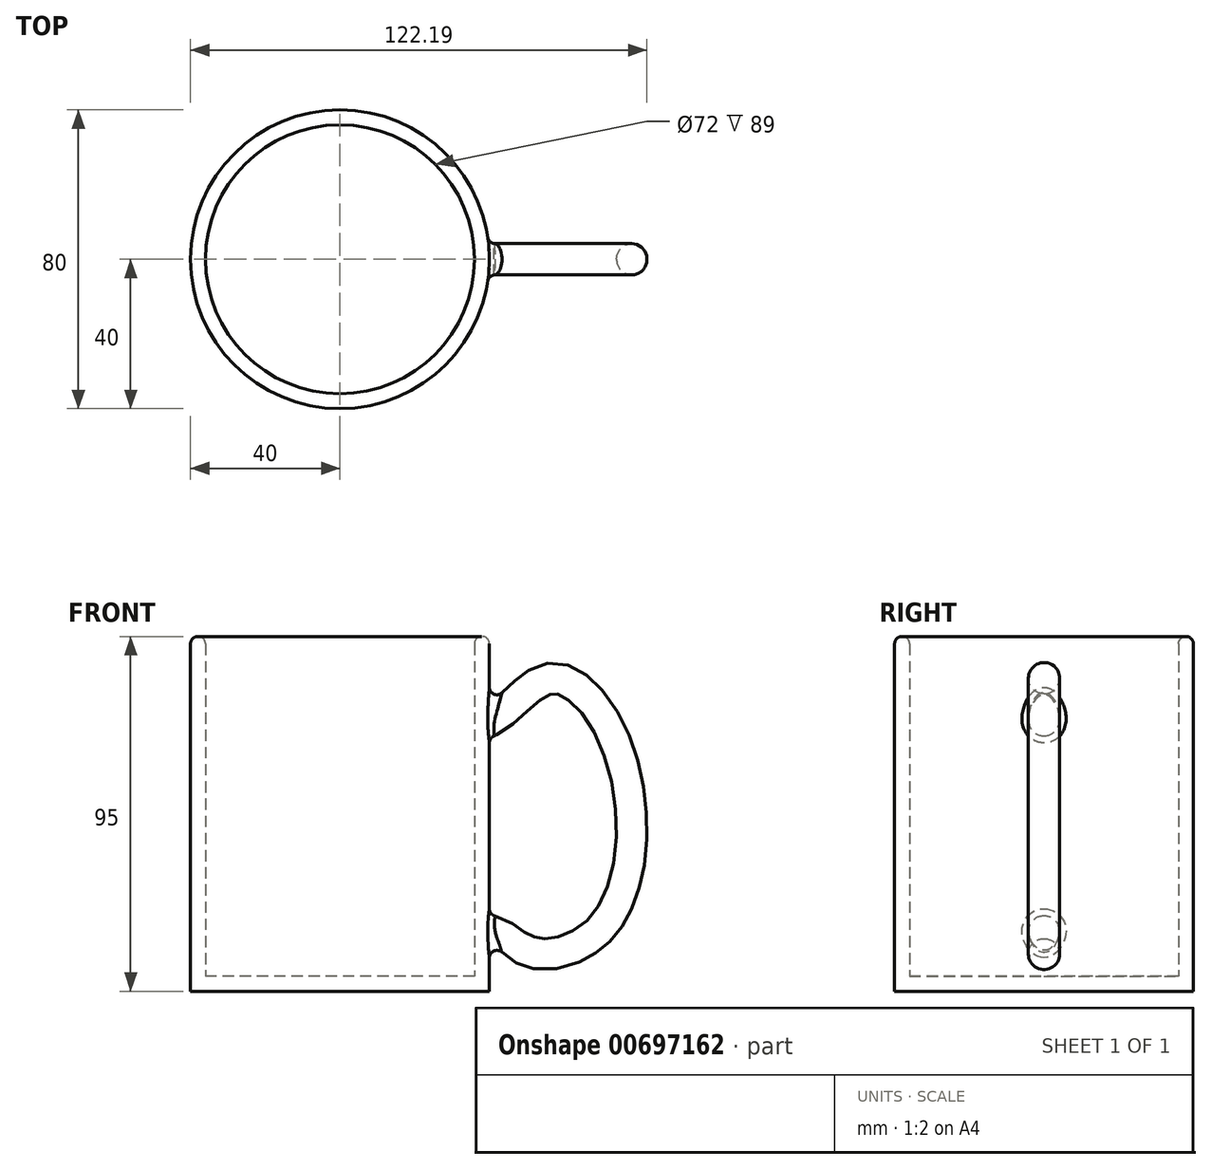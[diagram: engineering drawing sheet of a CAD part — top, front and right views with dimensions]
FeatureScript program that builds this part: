
annotation { "Feature Type Name" : "Feature", "Feature Type Description" : "" }
export const myFeature = defineFeature(function(context is Context, id is Id, definition is map)
    precondition{}
    {
        {
            var Q0;
            Q0=qCreatedBy(makeId("Top.planeOp"),FACE);
            var sketch = newSketch(context, id + "F0", { "sketchPlane" : qUnion([Q0])});
            skCircle(sketch, "E0", {"center": v(0, 0) * mm, "radius": 40 * mm});
            skSolve(sketch);
        }
        {
            var Q0;
            Q0 = qSketchRegion(id + "F0", true);
            extrude(context, id + "F1", {"entities" : qUnion([Q0]), "depth" : 95 * mm, "offsetDistance" : 25 * mm});
        }
        {
            var Q0;
            Q0=qCreatedBy(makeId("Front.planeOp"),FACE);
            var sketch = newSketch(context, id + "F2", { "sketchPlane" : qUnion([Q0])});
            skFitSpline(sketch, "E1", {"points": [v(32.9, 72.73) * mm, v(40.58, 72.94) * mm, v(56.34, 84.02) * mm, v(75.3, 63.57) * mm, v(71.46, 18.2) * mm, v(51.23, 10.1) * mm, v(40.36, 15.86) * mm, v(33.76, 16.07) * mm, v(33.97, 16.5) * mm], "startDerivative": vector(80.58, -21.73) * mm, "endDerivative": vector(19.6, 22.47) * mm});
            skSolve(sketch);
        }
        {
            var Q0;
            Q0=qCreatedBy(makeId("Right.planeOp"),FACE);
            cPlane(context, id + "F3", {"entities" : qUnion([Q0]), "cplaneType" : CPlaneType.OFFSET, "offset" : 31.4 * mm, "width" : 150 * mm, "height" : 150 * mm});
        }
        {
            var Q0;
            Q0=qCreatedBy(id+"F3.planeOp",FACE);
            var sketch = newSketch(context, id + "F4", { "sketchPlane" : qUnion([Q0])});
            skCircle(sketch, "E2", {"center": v(0, 72.73) * mm, "radius": 4.2 * mm});
            skSolve(sketch);
        }
        {
            var Q0;
            Q0 = qSketchRegion(id + "F4", true);
            var Q1;
            Q1 = qConstructionFilter(qBodyType(qCreatedBy(id + "F2" ,EDGE), BodyType.WIRE), ConstructionObject.NO);
            sweep(context, id + "F5", {"operationType" : NewBodyOperationType.ADD, "profiles" : qUnion([Q0]), "path" : qUnion([Q1])});
        }
        {
            var Q0;
            Q0=makeQuery(id+"F1.opExtrude","CAP_FACE",FACE,{"disambiguationData":[OSD([sQuery(id+"F0.wireOp",EDGE,"E0")])],"isStart":false});
            shell(context, id + "F6", {"entities" : qUnion([Q0]), "thickness" : 4 * mm});
        }
        {
            var Q0;
            {var subQ0=sQuery(id+"F0.wireOp",EDGE,"E0");Q0=makeQuery(id+"F6.opShell","OFFSET_EDGE",EDGE,{"disambiguationData":[OSD([subQ0]),TDD([makeQuery(id+"F1.opExtrude","CAP_EDGE",EDGE,{"disambiguationData":[OSD([subQ0])],"isStart":false})])]});}
            var Q1;
            Q1=makeQuery(id+"F1.opExtrude","CAP_EDGE",EDGE,{"disambiguationData":[OSD([sQuery(id+"F0.wireOp",EDGE,"E0")])],"isStart":false});
            var Q2;
            Q2=makeQuery(id+"F5.boolean.opBoolean","INTERSECT",EDGE,{"disambiguationData":[OD(1.0)],"derivedFrom":[makeQuery(id+"F1.opExtrude","SWEPT_FACE",FACE,{"disambiguationData":[OSD([sQuery(id+"F0.wireOp",EDGE,"E0")])]}),makeQuery(id+"F5.opSweep","SWEPT_FACE",FACE,{"disambiguationData":[OSD([sQuery(id+"F2.wireOp",EDGE,"E1"),sQuery(id+"F4.wireOp",EDGE,"E2")])]})]});
            var Q3;
            Q3=makeQuery(id+"F5.boolean.opBoolean","INTERSECT",EDGE,{"disambiguationData":[OD(0.0)],"derivedFrom":[makeQuery(id+"F1.opExtrude","SWEPT_FACE",FACE,{"disambiguationData":[OSD([sQuery(id+"F0.wireOp",EDGE,"E0")])]}),makeQuery(id+"F5.opSweep","SWEPT_FACE",FACE,{"disambiguationData":[OSD([sQuery(id+"F2.wireOp",EDGE,"E1"),sQuery(id+"F4.wireOp",EDGE,"E2")])]})]});
            fillet(context, id + "F7", {"entities" : qUnion([Q0, Q1, Q2, Q3]), "radius" : 2 * mm, "tangentPropagation" : true, "allowEdgeOverflow" : false});
        }
    });
